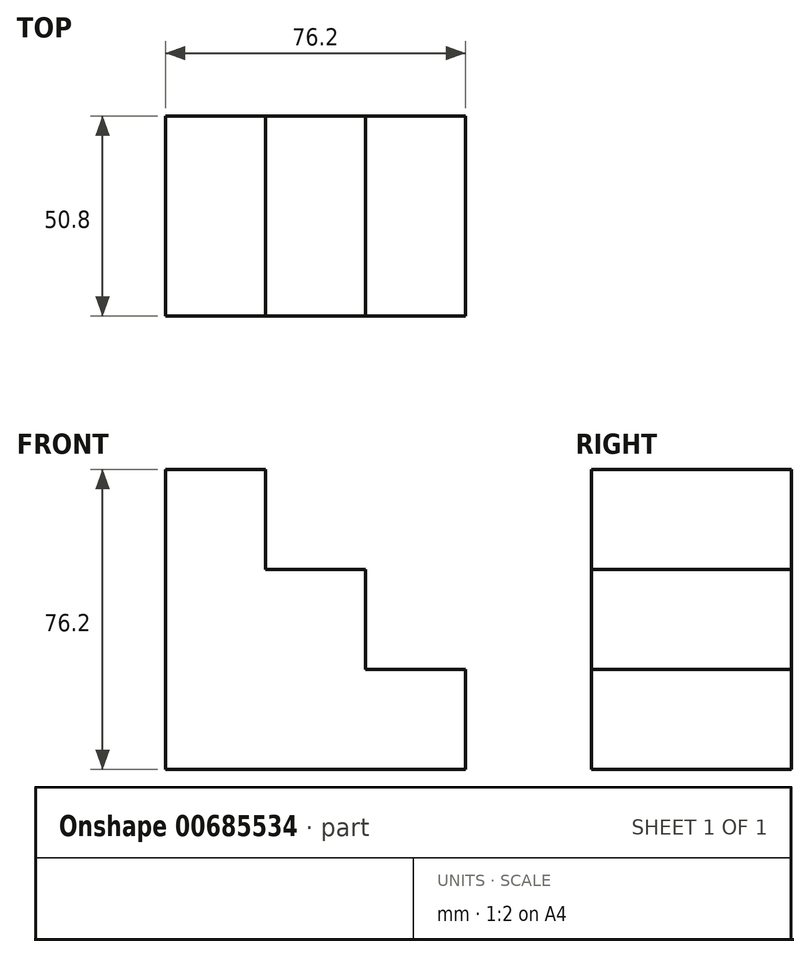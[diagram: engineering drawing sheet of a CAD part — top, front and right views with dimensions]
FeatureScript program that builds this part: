
annotation { "Feature Type Name" : "Feature", "Feature Type Description" : "" }
export const myFeature = defineFeature(function(context is Context, id is Id, definition is map)
    precondition{}
    {
        {
            var Q0;
            Q0=qCreatedBy(makeId("Front.planeOp"),FACE);
            var sketch = newSketch(context, id + "F0", { "sketchPlane" : qUnion([Q0])});
            skPoint(sketch, "E0.start.orphan", {"position": v(2.36, 0) * mm});
            skLineSegment(sketch, "E1", {"start": v(0, 0) * mm, "end": v(-76.2, 0) * mm});
            skLineSegment(sketch, "E2", {"start": v(-76.2, 0) * mm, "end": v(-76.2, 76.2) * mm});
            skLineSegment(sketch, "E3", {"start": v(-76.2, 76.2) * mm, "end": v(-50.8, 76.2) * mm});
            skLineSegment(sketch, "E4", {"start": v(-50.8, 76.2) * mm, "end": v(-50.8, 50.8) * mm});
            skLineSegment(sketch, "E5", {"start": v(-50.8, 50.8) * mm, "end": v(-25.4, 50.8) * mm});
            skLineSegment(sketch, "E6", {"start": v(-25.4, 50.8) * mm, "end": v(-25.4, 25.4) * mm});
            skLineSegment(sketch, "E7", {"start": v(-25.4, 25.4) * mm, "end": v(0, 25.4) * mm});
            skLineSegment(sketch, "E8", {"start": v(0, 25.4) * mm, "end": v(0, 0) * mm});
            skSolve(sketch);
        }
        {
            var Q0;
            Q0=makeQuery(id+"F0.imprint","IMPRINT",FACE,{"disambiguationData":[TD([[makeQuery(id+"F0.imprint","IMPRINT",EDGE,{"derivedFrom":sQuery(id+"F0.wireOp",EDGE,"E1")}),-1.0]])]});
            extrude(context, id + "F1", {"entities" : qUnion([Q0]), "depth" : 50.8 * mm, "offsetDistance" : 25.4 * mm});
        }
    });
